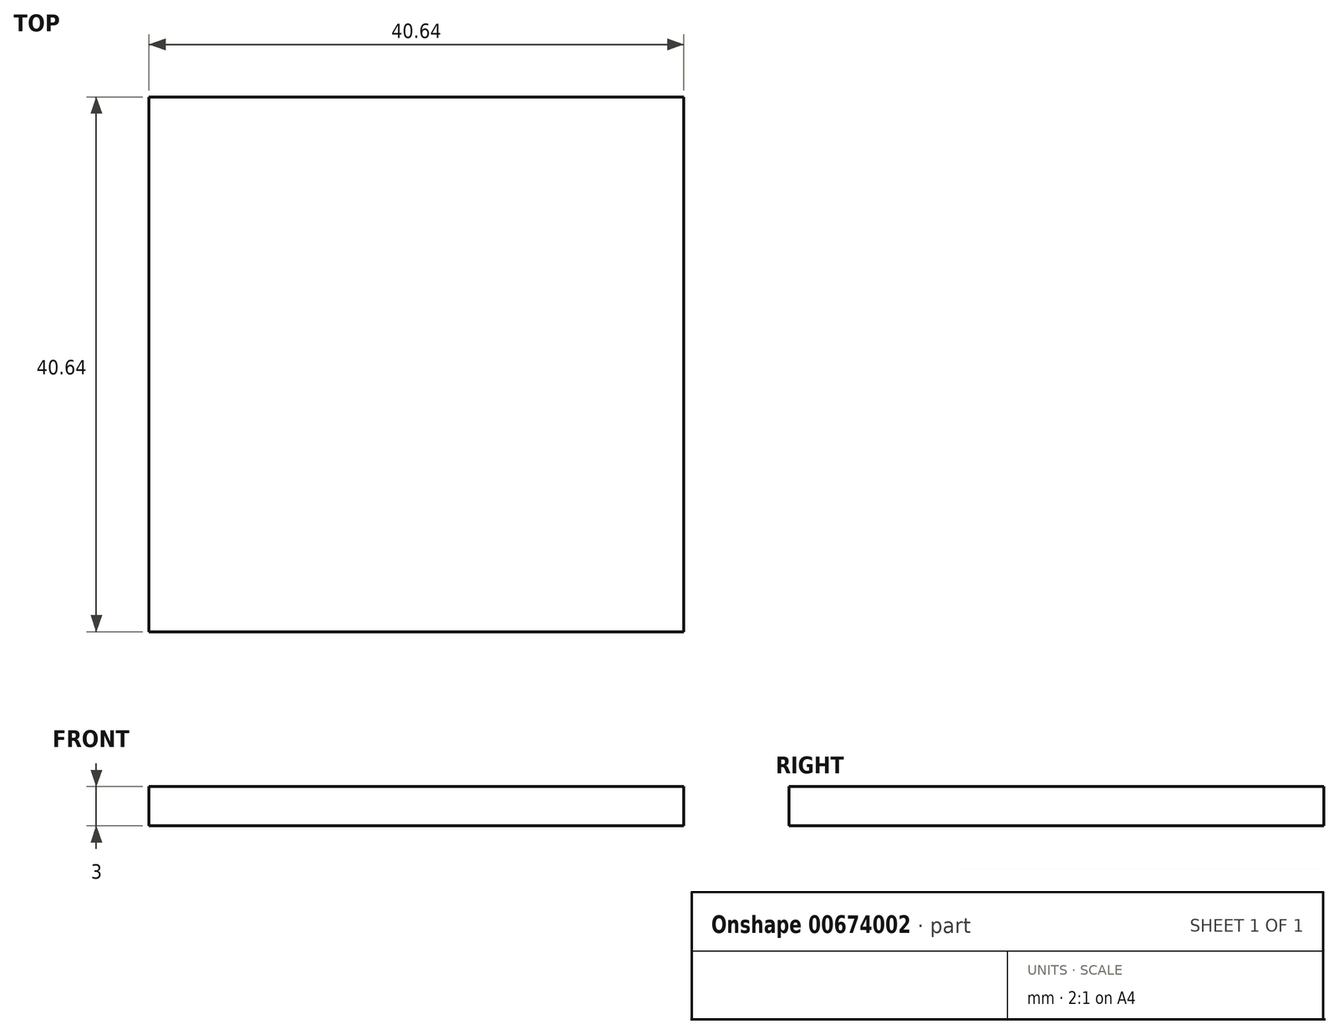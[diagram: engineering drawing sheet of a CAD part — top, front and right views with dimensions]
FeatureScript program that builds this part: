
annotation { "Feature Type Name" : "Feature", "Feature Type Description" : "" }
export const myFeature = defineFeature(function(context is Context, id is Id, definition is map)
    precondition{}
    {
        {
            var Q0;
            Q0=qCreatedBy(makeId("Top.planeOp"),FACE);
            var sketch = newSketch(context, id + "F0", { "sketchPlane" : qUnion([Q0])});
            skLineSegment(sketch, "E0.bottom", {"start": v(-40.64, 35.15) * mm, "end": v(0, 35.15) * mm});
            skLineSegment(sketch, "E0.top", {"start": v(-40.64, -5.49) * mm, "end": v(0, -5.49) * mm});
            skLineSegment(sketch, "E0.left", {"start": v(-40.64, 35.15) * mm, "end": v(-40.64, -5.49) * mm});
            skLineSegment(sketch, "E0.right", {"start": v(0, 35.15) * mm, "end": v(0, -5.49) * mm});
            skSolve(sketch);
        }
        {
            var Q0;
            Q0=makeQuery(id+"F0.imprint","IMPRINT",FACE,{"disambiguationData":[TD([[makeQuery(id+"F0.imprint","IMPRINT",EDGE,{"derivedFrom":sQuery(id+"F0.wireOp",EDGE,"E0.bottom")}),-1.0]])]});
            extrude(context, id + "F1", {"entities" : qUnion([Q0]), "depth" : 3 * mm, "offsetDistance" : 25.4 * mm});
        }
    });
